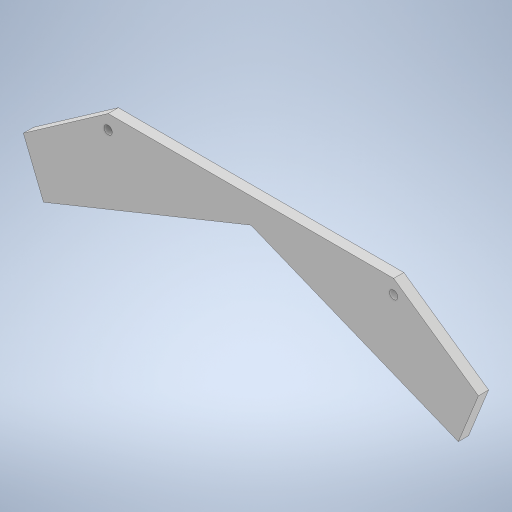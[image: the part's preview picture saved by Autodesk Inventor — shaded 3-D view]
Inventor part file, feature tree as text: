
AUTODESK INVENTOR PART (.ipt)
format: ipt  version: 2024 (Build 280153000, 153)  size: 259,072 bytes
history: native  units: mm
features: extrude x3, sketch x3, other x1
ambient origin geometry x8: Origin, YZ Plane, XZ Plane, XY Plane, X Axis, Y Axis, Z Axis, Center Point
bodies: Body1 (feature_tree)
feature tree (7):
  other  "Těleso1"
  extrude  "Vysunutí1"  Depth=140.0mm
  extrude  "Vysunutí2"  Depth=81.0mm
  extrude  "Vysunutí3"  Depth=6.108652mm
  sketch  "Náčrt1"
  sketch  "Náčrt2"
  sketch  "Náčrt4"
